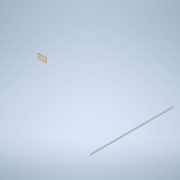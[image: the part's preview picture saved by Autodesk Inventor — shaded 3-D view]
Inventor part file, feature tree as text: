
AUTODESK INVENTOR PART (.ipt)
format: ipt  version: 2021 (Build 250183000, 183)  size: 103,424 bytes
history: native  units: mm
features: other x4, extrude x1, chamfer x1, reference x1
ambient origin geometry x8: Origin, YZ Plane, XZ Plane, XY Plane, X Axis, Y Axis, Z Axis, Center Point
bodies: Body1 (feature_tree)
feature tree (7):
  other  "Bryła1"
  other  "Płaszczyzna konstrukcyjna1"
  extrude  "Wyciągnięcie proste1"  Depth=230.0mm TaperAngle=0.0deg
  chamfer  "Faza1"  Distance=2.0mm Angle=45.0deg
  reference  "Odniesienie1"
  other  "cw12model.iam"
  other  "shaft:1"
